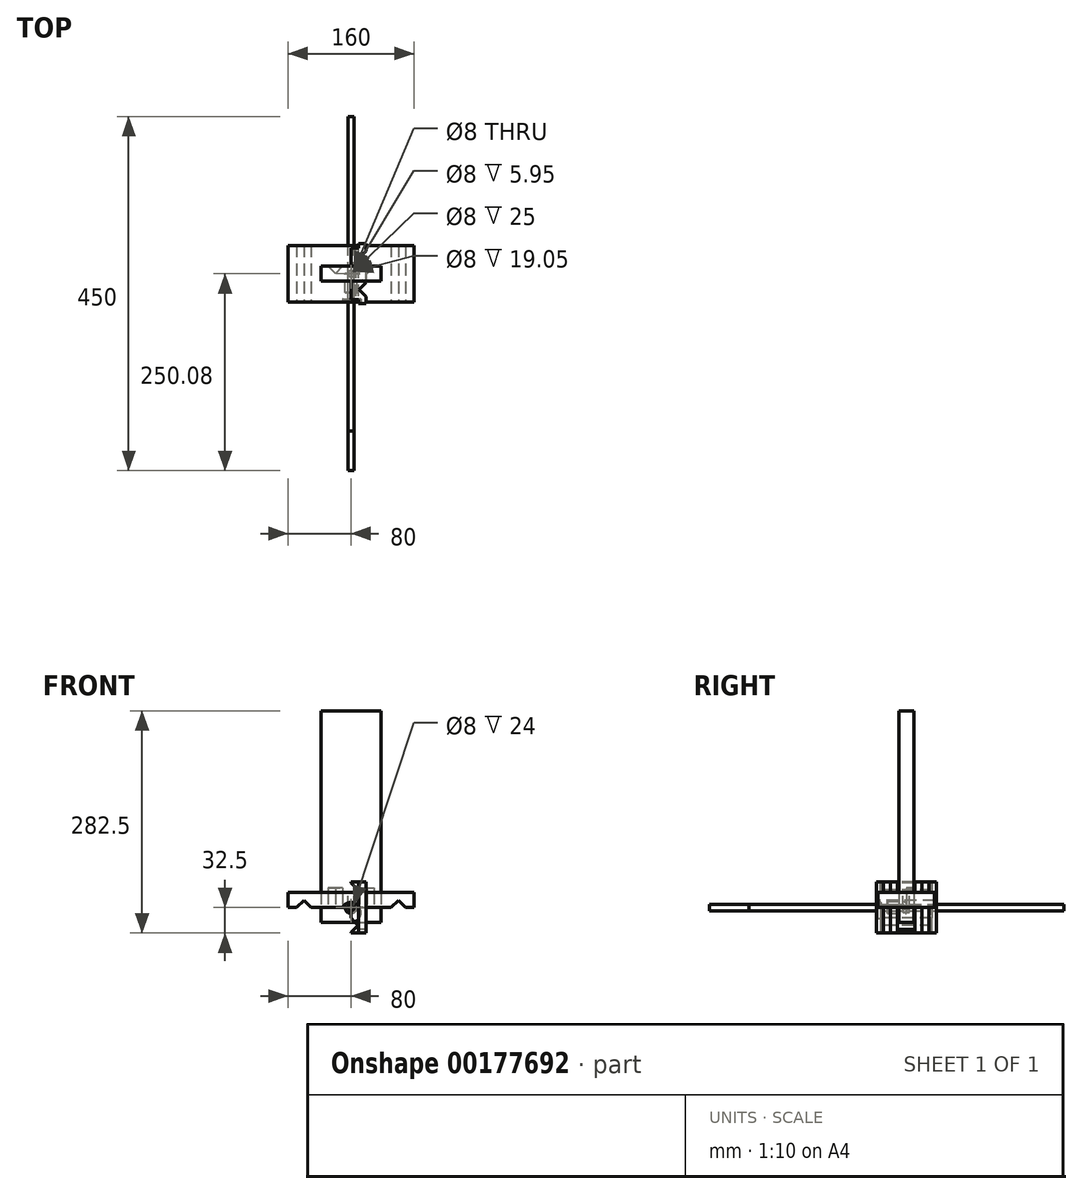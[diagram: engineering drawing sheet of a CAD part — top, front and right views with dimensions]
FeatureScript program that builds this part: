
annotation { "Feature Type Name" : "Feature", "Feature Type Description" : "" }
export const myFeature = defineFeature(function(context is Context, id is Id, definition is map)
    precondition{}
    {
        {
            var Q0;
            Q0=qCreatedBy(makeId("Front.planeOp"),FACE);
            var sketch = newSketch(context, id + "F0", { "sketchPlane" : qUnion([Q0])});
            skCircle(sketch, "E0", {"center": v(0, 0) * mm, "radius": 4 * mm});
            skCircle(sketch, "E1", {"center": v(0, 0) * mm, "radius": 7.5 * mm});
            skSolve(sketch);
        }
        {
            var Q0;
            Q0 = qSketchRegion(id + "F0", true);
            extrude(context, id + "F1", {"entities" : qUnion([Q0]), "depth" : 24 * mm});
        }
        {
            var Q0;
            Q0=qCreatedBy(makeId("Front.planeOp"),FACE);
            var sketch = newSketch(context, id + "F2", { "sketchPlane" : qUnion([Q0])});
            skCircle(sketch, "E2", {"center": v(0, 0) * mm, "radius": 4 * mm});
            skSolve(sketch);
        }
        {
            var Q0;
            Q0 = qSketchRegion(id + "F2", true);
            extrude(context, id + "F3", {"entities" : qUnion([Q0]), "endBound" : BoundingType.SYMMETRIC, "depth" : 400 * mm});
        }
        {
            var Q0;
            Q0=qCreatedBy(makeId("Front.planeOp"),FACE);
            var sketch = newSketch(context, id + "F4", { "sketchPlane" : qUnion([Q0])});
            skCircle(sketch, "E3", {"center": v(0, 0) * mm, "radius": 4 * mm});
            skSolve(sketch);
        }
        {
            var Q0;
            Q0 = qSketchRegion(id + "F4", true);
            extrude(context, id + "F5", {"entities" : qUnion([Q0]), "depth" : 250 * mm});
        }
        {
            var Q0;
            Q0=qCreatedBy(makeId("Right.planeOp"),FACE);
            var sketch = newSketch(context, id + "F6", { "sketchPlane" : qUnion([Q0])});
            skLineSegment(sketch, "E4.bottom", {"start": v(32.5, 32.5) * mm, "end": v(-32.5, 32.5) * mm});
            skLineSegment(sketch, "E4.top", {"start": v(32.5, -32.5) * mm, "end": v(-32.5, -32.5) * mm});
            skLineSegment(sketch, "E4.left", {"start": v(32.5, 32.5) * mm, "end": v(32.5, -32.5) * mm});
            skLineSegment(sketch, "E4.right", {"start": v(-32.5, 32.5) * mm, "end": v(-32.5, -32.5) * mm});
            skPoint(sketch, "E4.middle", {"position": v(0, 0) * mm});
            skSolve(sketch);
        }
        {
            var Q0;
            Q0 = qSketchRegion(id + "F6", true);
            extrude(context, id + "F7", {"entities" : qUnion([Q0]), "depth" : 19.05 * mm});
        }
        {
            var Q0;
            Q0=makeQuery(id+"F7.opExtrude","SWEPT_FACE",FACE,{"disambiguationData":[OSD([sQuery(id+"F6.wireOp",EDGE,"E4.right")])]});
            var sketch = newSketch(context, id + "F8", { "sketchPlane" : qUnion([Q0])});
            skLineSegment(sketch, "E5", {"start": v(0, 0) * mm, "end": v(0, 13.5) * mm, "construction": true});
            skLineSegment(sketch, "E6", {"start": v(0, 13.5) * mm, "end": v(9, 22.5) * mm});
            skLineSegment(sketch, "E7", {"start": v(9, 22.5) * mm, "end": v(0, 31.5) * mm});
            skLineSegment(sketch, "E8", {"start": v(0, 31.5) * mm, "end": v(0, 13.5) * mm});
            skLineSegment(sketch, "E9", {"start": v(0, 0) * mm, "end": v(-31.4, 0) * mm, "construction": true});
            skLineSegment(sketch, "E10.MirrorCS", {"start": v(0, -13.5) * mm, "end": v(9, -22.5) * mm});
            skLineSegment(sketch, "E11.MirrorCS", {"start": v(9, -22.5) * mm, "end": v(0, -31.5) * mm});
            skLineSegment(sketch, "E12.MirrorCS", {"start": v(0, -31.5) * mm, "end": v(0, -13.5) * mm});
            skLineSegment(sketch, "E13.MirrorCS", {"start": v(0, 0) * mm, "end": v(0, -13.5) * mm, "construction": true});
            skSolve(sketch);
        }
        {
            var Q0;
            Q0 = qSketchRegion(id + "F8", true);
            extrude(context, id + "F9", {"entities" : qUnion([Q0]), "operationType" : NewBodyOperationType.REMOVE, "endBound" : BoundingType.THROUGH_ALL, "oppositeDirection" : true, "depth" : 25 * mm});
        }
        {
            var Q0;
            Q0=makeQuery(id+"F7.opExtrude","SWEPT_FACE",FACE,{"disambiguationData":[OSD([sQuery(id+"F6.wireOp",EDGE,"E4.bottom")])]});
            var sketch = newSketch(context, id + "F10", { "sketchPlane" : qUnion([Q0])});
            skLineSegment(sketch, "E14", {"start": v(19.05, 0) * mm, "end": v(19.05, 11) * mm, "construction": true});
            skLineSegment(sketch, "E15", {"start": v(19.05, 11) * mm, "end": v(10.05, 20) * mm});
            skLineSegment(sketch, "E16", {"start": v(10.05, 20) * mm, "end": v(19.05, 29) * mm});
            skLineSegment(sketch, "E17", {"start": v(19.05, 29) * mm, "end": v(19.05, 11) * mm});
            skLineSegment(sketch, "E18", {"start": v(19.05, 0) * mm, "end": v(42.03, 0) * mm, "construction": true});
            skLineSegment(sketch, "E19.MirrorCS", {"start": v(19.05, 0) * mm, "end": v(19.05, -11) * mm, "construction": true});
            skLineSegment(sketch, "E20.MirrorCS", {"start": v(19.05, -11) * mm, "end": v(10.05, -20) * mm});
            skLineSegment(sketch, "E21.MirrorCS", {"start": v(10.05, -20) * mm, "end": v(19.05, -29) * mm});
            skLineSegment(sketch, "E22.MirrorCS", {"start": v(19.05, -29) * mm, "end": v(19.05, -11) * mm});
            skSolve(sketch);
        }
        {
            var Q0;
            Q0 = qSketchRegion(id + "F10", true);
            extrude(context, id + "F11", {"entities" : qUnion([Q0]), "operationType" : NewBodyOperationType.REMOVE, "endBound" : BoundingType.THROUGH_ALL, "oppositeDirection" : true, "depth" : 25 * mm});
        }
        {
            var Q0;
            Q0=qCreatedBy(makeId("Top.planeOp"),FACE);
            var sketch = newSketch(context, id + "F12", { "sketchPlane" : qUnion([Q0])});
            skLineSegment(sketch, "E23.bottom", {"start": v(38.1, -9.52) * mm, "end": v(-38.1, -9.53) * mm});
            skLineSegment(sketch, "E23.top", {"start": v(38.1, 9.53) * mm, "end": v(-38.1, 9.52) * mm});
            skLineSegment(sketch, "E23.left", {"start": v(38.1, -9.52) * mm, "end": v(38.1, 9.53) * mm});
            skLineSegment(sketch, "E23.right", {"start": v(-38.1, -9.53) * mm, "end": v(-38.1, 9.52) * mm});
            skPoint(sketch, "E23.middle", {"position": v(0, 0) * mm});
            skSolve(sketch);
        }
        {
            var Q0;
            Q0 = qSketchRegion(id + "F12", true);
            extrude(context, id + "F13", {"entities" : qUnion([Q0]), "depth" : 250 * mm});
        }
        {
            var Q0;
            Q0=qCreatedBy(makeId("Top.planeOp"),FACE);
            var sketch = newSketch(context, id + "F14", { "sketchPlane" : qUnion([Q0])});
            skLineSegment(sketch, "E24.bottom", {"start": v(38.1, -9.53) * mm, "end": v(-38.1, -9.53) * mm});
            skLineSegment(sketch, "E24.top", {"start": v(38.1, 9.53) * mm, "end": v(-38.1, 9.53) * mm});
            skLineSegment(sketch, "E24.left", {"start": v(38.1, -9.53) * mm, "end": v(38.1, 9.53) * mm});
            skLineSegment(sketch, "E24.right", {"start": v(-38.1, -9.53) * mm, "end": v(-38.1, 9.53) * mm});
            skPoint(sketch, "E24.middle", {"position": v(0, 0) * mm});
            skSolve(sketch);
        }
        {
            var Q0;
            Q0 = qSketchRegion(id + "F14", true);
            extrude(context, id + "F15", {"entities" : qUnion([Q0]), "depth" : 19.05 * mm});
        }
        {
            var Q0;
            Q0=makeQuery(id+"F15.opExtrude","CAP_FACE",FACE,{"disambiguationData":[OSD([sQuery(id+"F14.wireOp",EDGE,"E24.bottom"),sQuery(id+"F14.wireOp",EDGE,"E24.top"),sQuery(id+"F14.wireOp",EDGE,"E24.left"),sQuery(id+"F14.wireOp",EDGE,"E24.right")])],"isStart":true});
            var sketch = newSketch(context, id + "F16", { "sketchPlane" : qUnion([Q0])});
            skLineSegment(sketch, "E25", {"start": v(0, -9.53) * mm, "end": v(11, -9.53) * mm, "construction": true});
            skLineSegment(sketch, "E26", {"start": v(11, -9.53) * mm, "end": v(20, -0.53) * mm});
            skLineSegment(sketch, "E27", {"start": v(20, -0.53) * mm, "end": v(29, -9.53) * mm});
            skLineSegment(sketch, "E28", {"start": v(29, -9.53) * mm, "end": v(11, -9.53) * mm});
            skLineSegment(sketch, "E29", {"start": v(0, -9.53) * mm, "end": v(0, -27.73) * mm, "construction": true});
            skLineSegment(sketch, "E30.MirrorCS", {"start": v(0, -9.53) * mm, "end": v(-11, -9.53) * mm, "construction": true});
            skLineSegment(sketch, "E31.MirrorCS", {"start": v(-11, -9.53) * mm, "end": v(-20, -0.53) * mm});
            skLineSegment(sketch, "E32.MirrorCS", {"start": v(-20, -0.53) * mm, "end": v(-29, -9.53) * mm});
            skLineSegment(sketch, "E33.MirrorCS", {"start": v(-29, -9.53) * mm, "end": v(-11, -9.53) * mm});
            skSolve(sketch);
        }
        {
            var Q0;
            Q0 = qSketchRegion(id + "F16", true);
            extrude(context, id + "F17", {"entities" : qUnion([Q0]), "operationType" : NewBodyOperationType.REMOVE, "oppositeDirection" : true, "depth" : 25 * mm});
        }
        {
            var Q0;
            Q0=qCreatedBy(makeId("Top.planeOp"),FACE);
            var sketch = newSketch(context, id + "F18", { "sketchPlane" : qUnion([Q0])});
            skLineSegment(sketch, "E34.bottom", {"start": v(80, -36) * mm, "end": v(-80, -36) * mm});
            skLineSegment(sketch, "E34.top", {"start": v(80, 36) * mm, "end": v(-80, 36) * mm});
            skLineSegment(sketch, "E34.left", {"start": v(80, -36) * mm, "end": v(80, 36) * mm});
            skLineSegment(sketch, "E34.right", {"start": v(-80, -36) * mm, "end": v(-80, 36) * mm});
            skPoint(sketch, "E34.middle", {"position": v(0, 0) * mm});
            skSolve(sketch);
        }
        {
            var Q0;
            Q0 = qSketchRegion(id + "F18", true);
            extrude(context, id + "F19", {"entities" : qUnion([Q0]), "depth" : 19.05 * mm});
        }
        {
            var Q0;
            Q0=makeQuery(id+"F19.opExtrude","SWEPT_FACE",FACE,{"disambiguationData":[OSD([sQuery(id+"F18.wireOp",EDGE,"E34.bottom")])]});
            var sketch = newSketch(context, id + "F20", { "sketchPlane" : qUnion([Q0])});
            skLineSegment(sketch, "E35", {"start": v(0, 0) * mm, "end": v(51, 0) * mm, "construction": true});
            skLineSegment(sketch, "E36", {"start": v(51, 0) * mm, "end": v(60, 9) * mm});
            skLineSegment(sketch, "E37", {"start": v(60, 9) * mm, "end": v(69, 0) * mm});
            skLineSegment(sketch, "E38", {"start": v(69, 0) * mm, "end": v(51, 0) * mm});
            skLineSegment(sketch, "E39", {"start": v(0, 0) * mm, "end": v(0, -15.8) * mm, "construction": true});
            skLineSegment(sketch, "E40.MirrorCS", {"start": v(0, 0) * mm, "end": v(-51, 0) * mm, "construction": true});
            skLineSegment(sketch, "E41.MirrorCS", {"start": v(-51, 0) * mm, "end": v(-60, 9) * mm});
            skLineSegment(sketch, "E42.MirrorCS", {"start": v(-60, 9) * mm, "end": v(-69, 0) * mm});
            skLineSegment(sketch, "E43.MirrorCS", {"start": v(-69, 0) * mm, "end": v(-51, 0) * mm});
            skSolve(sketch);
        }
        {
            var Q0;
            Q0 = qSketchRegion(id + "F20", true);
            extrude(context, id + "F21", {"entities" : qUnion([Q0]), "operationType" : NewBodyOperationType.REMOVE, "endBound" : BoundingType.THROUGH_ALL, "oppositeDirection" : true, "depth" : 25 * mm});
        }
        {
            var Q0;
            Q0=qCreatedBy(makeId("Top.planeOp"),FACE);
            var sketch = newSketch(context, id + "F22", { "sketchPlane" : qUnion([Q0])});
            skLineSegment(sketch, "E44.bottom", {"start": v(-38.1, -9.53) * mm, "end": v(38.1, -9.53) * mm});
            skLineSegment(sketch, "E44.top", {"start": v(-38.1, 9.53) * mm, "end": v(38.1, 9.53) * mm});
            skLineSegment(sketch, "E44.left", {"start": v(-38.1, -9.53) * mm, "end": v(-38.1, 9.53) * mm});
            skLineSegment(sketch, "E44.right", {"start": v(38.1, -9.53) * mm, "end": v(38.1, 9.53) * mm});
            skPoint(sketch, "E44.middle", {"position": v(0, 0) * mm});
            skSolve(sketch);
        }
        {
            var Q0;
            Q0 = qSketchRegion(id + "F22", true);
            extrude(context, id + "F23", {"entities" : qUnion([Q0]), "oppositeDirection" : true, "depth" : 19.05 * mm});
        }
        {
            var Q0;
            Q0=makeQuery(id+"F7.opExtrude","SWEPT_FACE",FACE,{"disambiguationData":[OSD([sQuery(id+"F6.wireOp",EDGE,"E4.right")])]});
            var sketch = newSketch(context, id + "F24", { "sketchPlane" : qUnion([Q0])});
            skLineSegment(sketch, "E45.bottom", {"start": v(19.05, 32.5) * mm, "end": v(9.53, 32.5) * mm});
            skLineSegment(sketch, "E45.top", {"start": v(19.05, -32.5) * mm, "end": v(9.53, -32.5) * mm});
            skLineSegment(sketch, "E45.left", {"start": v(19.05, 32.5) * mm, "end": v(19.05, -32.5) * mm});
            skLineSegment(sketch, "E45.right", {"start": v(9.53, 32.5) * mm, "end": v(9.53, -32.5) * mm});
            skSolve(sketch);
        }
        {
            var Q0;
            Q0 = qSketchRegion(id + "F24", true);
            extrude(context, id + "F25", {"entities" : qUnion([Q0]), "operationType" : NewBodyOperationType.ADD, "depth" : 5.6 * mm});
        }
        {
            var Q0;
            Q0=makeQuery(id+"F7.opExtrude","SWEPT_FACE",FACE,{"disambiguationData":[OSD([sQuery(id+"F6.wireOp",EDGE,"E4.left")])]});
            var sketch = newSketch(context, id + "F26", { "sketchPlane" : qUnion([Q0])});
            skLineSegment(sketch, "E46.bottom", {"start": v(-19.05, -32.5) * mm, "end": v(-9.53, -32.5) * mm});
            skLineSegment(sketch, "E46.top", {"start": v(-19.05, 32.5) * mm, "end": v(-9.53, 32.5) * mm});
            skLineSegment(sketch, "E46.left", {"start": v(-19.05, -32.5) * mm, "end": v(-19.05, 32.5) * mm});
            skLineSegment(sketch, "E46.right", {"start": v(-9.53, -32.5) * mm, "end": v(-9.53, 32.5) * mm});
            skSolve(sketch);
        }
        {
            var Q0;
            Q0 = qSketchRegion(id + "F26", true);
            extrude(context, id + "F27", {"entities" : qUnion([Q0]), "operationType" : NewBodyOperationType.ADD, "depth" : 5.6 * mm});
        }
        {
            var Q0;
            Q0=makeQuery(id+"F15.opExtrude","CAP_FACE",FACE,{"disambiguationData":[OSD([sQuery(id+"F14.wireOp",EDGE,"E24.bottom"),sQuery(id+"F14.wireOp",EDGE,"E24.top"),sQuery(id+"F14.wireOp",EDGE,"E24.left"),sQuery(id+"F14.wireOp",EDGE,"E24.right")])],"isStart":false});
            var sketch = newSketch(context, id + "F28", { "sketchPlane" : qUnion([Q0])});
            skLineSegment(sketch, "E47", {"start": v(0, -9.53) * mm, "end": v(0, 0.08) * mm, "construction": true});
            skPoint(sketch, "E47.endSnap0", {"position": v(0, -9.53) * mm});
            skCircle(sketch, "E48", {"center": v(0, 0.08) * mm, "radius": 4 * mm});
            skSolve(sketch);
        }
        {
            var Q0;
            Q0=makeQuery(id+"F28.imprint","IMPRINT",FACE,{"disambiguationData":[TD([[makeQuery(id+"F28.imprint","IMPRINT",EDGE,{"derivedFrom":sQuery(id+"F28.wireOp",EDGE,"E48")}),1.0]])]});
            var Q1;
            Q1=sQuery(id+"F28.wireOp",EDGE,"E47");
            var Q2;
            Q2=sQuery(id+"F28.wireOp",EDGE,"E48");
            extrude(context, id + "F29", {"entities" : qUnion([Q0]), "operationType" : NewBodyOperationType.REMOVE, "surfaceEntities" : qUnion([Q1, Q2]), "oppositeDirection" : true, "depth" : 25 * mm});
        }
        {
            var Q0;
            Q0=makeQuery(id+"F27.boolean.opBoolean","MERGE",FACE,{"derivedFrom":[makeQuery(id+"F25.boolean.opBoolean","MERGE",FACE,{"derivedFrom":[makeQuery(id+"F7.opExtrude","SWEPT_FACE",FACE,{"disambiguationData":[OSD([sQuery(id+"F6.wireOp",EDGE,"E4.top")])]}),makeQuery(id+"F25.opExtrude","SWEPT_FACE",FACE,{"disambiguationData":[OSD([sQuery(id+"F24.wireOp",EDGE,"E45.top")])]})]}),makeQuery(id+"F27.opExtrude","SWEPT_FACE",FACE,{"disambiguationData":[OSD([sQuery(id+"F26.wireOp",EDGE,"E46.bottom")])]})]});
            var sketch = newSketch(context, id + "F30", { "sketchPlane" : qUnion([Q0])});
            skCircle(sketch, "E49", {"center": v(19.05, 0) * mm, "radius": 9 * mm});
            skSolve(sketch);
        }
        {
            var Q0;
            Q0 = qSketchRegion(id + "F30", true);
            extrude(context, id + "F31", {"entities" : qUnion([Q0]), "operationType" : NewBodyOperationType.REMOVE, "oppositeDirection" : true, "depth" : 5 * mm});
        }
        {
            var Q0;
            Q0=makeQuery(id+"F19.opExtrude","SWEPT_FACE",FACE,{"disambiguationData":[OSD([sQuery(id+"F18.wireOp",EDGE,"E34.bottom")])]});
            var sketch = newSketch(context, id + "F32", { "sketchPlane" : qUnion([Q0])});
            skLineSegment(sketch, "E50", {"start": v(0, 0) * mm, "end": v(0, -6.35) * mm, "construction": true});
            skCircle(sketch, "E51", {"center": v(0, -6.35) * mm, "radius": 12.7 * mm});
            skSolve(sketch);
        }
        {
            var Q0;
            {var subQ0=sQuery(id+"F32.wireOp",EDGE,"E51");var subQ1=sQuery(id+"F18.wireOp",EDGE,"E34.bottom");var subQ2=makeQuery(id+"F21.boolean.opBoolean","SPLIT",EDGE,{"disambiguationData":[TD([makeQuery(id+"F21.opExtrude","SWEPT_FACE",FACE,{"disambiguationData":[OSD([sQuery(id+"F20.wireOp",EDGE,"E36")])]})])],"derivedFrom":makeQuery(id+"F19.opExtrude","CAP_EDGE",EDGE,{"disambiguationData":[OSD([subQ1])],"isStart":true})});var subQ3=makeQuery(id+"F32.imprint","INTERSECT",VERTEX,{"disambiguationData":[OD(0.0)],"derivedFrom":[subQ2,subQ0]});Q0=makeQuery(id+"F32.imprint","IMPRINT",FACE,{"disambiguationData":[TD([[makeQuery(id+"F32.imprint","IMPRINT",EDGE,{"disambiguationData":[TD([[subQ3,-1.0]])],"derivedFrom":subQ0}),1.0]])]});}
            extrude(context, id + "F33", {"entities" : qUnion([Q0]), "operationType" : NewBodyOperationType.REMOVE, "oppositeDirection" : true, "depth" : 4 * mm});
        }
    });
